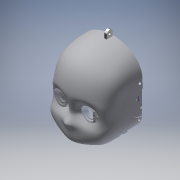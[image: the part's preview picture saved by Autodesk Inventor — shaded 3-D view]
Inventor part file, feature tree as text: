
AUTODESK INVENTOR PART (.ipt)
format: ipt  version: 2019 (Build 230136000, 136)  size: 8,056,320 bytes
history: native  units: in
note: dims shown in document units (in); Inventor stores cm internally (conversion verified against a paired STEP export)
features: sketch x29, extrude x22, other x18, plane x14, projected_geometry x7, mirror x6, surface_op x6, fillet x2, hole x2, thicken_offset x2, imported_body x2
ambient origin geometry x8: Origin, YZ Plane, XZ Plane, XY Plane, X Axis, Y Axis, Z Axis, Center Point
bodies: Solid6 (feature_tree), Solid2 (feature_tree)
feature tree (110):
  other  "rc_ist_009_p_077_09"
  other  "rc_ist_009_p_077_091"
  other  "Work Point1"
  other  "Work Point2"
  other  "Work Point3"
  other  "Work Point4"
  other  "Work Point5"
  other  "A_5"
  other  "A_6"
  other  "A_7"
  other  "A_8"
  other  "SIDE"
  other  "TOP"
  plane  "Work Plane4"
  plane  "Work Plane11"
  plane  "Work Plane7"
  plane  "Work Plane9"
  extrude  "Extrusion10"  Depth=0.9252in
  sketch  "Sketch11"  dims[d40=0.315in d41=0.315in]
  extrude  "Extrusion11"  Depth=0.315in
  plane  "Work Plane10"
  extrude  "Extrusion12"  Depth=1.063in TaperAngle=0.0deg
  mirror  "Mirror3"
  extrude  "Extrusion13"  Depth=1.8504in
  fillet  "Fillet1"  Radius=2.3622in
  fillet  "Fillet2"  Radius=0.3543in
  sketch  "Sketch15"  dims[d54=0.2756in d55=0.1969in d56=0.0in]
  extrude  "Extrusion14"  Depth=0.1969in TaperAngle=0.0deg
  extrude  "Extrusion15"  Depth=0.1969in TaperAngle=0.0deg
  extrude  "Extrusion16"  Depth=0.3937in
  extrude  "Extrusion17"  Depth=0.3937in
  extrude  "Extrusion18"  Depth=1.1811in
  extrude  "Extrusion19"  Depth=0.3937in
  hole  "Hole1"  [1 undecoded]
  hole  "Hole2"  [1 undecoded]
  extrude  "Extrusion22"  Depth=2.5591in
  extrude  "Extrusion23"  TaperAngle=150.0deg  [1 undecoded]
  extrude  "Extrusion24"  TaperAngle=60.0deg  [1 undecoded]
  extrude  "Extrusion25"  Depth=0.315in
  extrude  "Extrusion26"  Depth=0.3937in TaperAngle=0.0deg
  sketch  "Sketch34"  dims[d96=0.1969in d97=150.0deg]
  sketch  "3D Sketch2"
  surface_op  "Extend2"
  thicken_offset  "Thicken5"
  plane  "Work Plane12"
  extrude  "Extrusion27"  TaperAngle=150.0deg  [1 undecoded]
  plane  "Work Plane13"
  surface_op  "Extend3"
  thicken_offset  "Thicken6"
  mirror  "Mirror4"
  plane  "Work Plane14"
  plane  "Work Plane15"
  extrude  "Extrusion29"  TaperAngle=120.0deg  [1 undecoded]
  mirror  "Mirror5"
  plane  "Work Plane16"
  extrude  "Extrusion30"  TaperAngle=150.0deg  [1 undecoded]
  mirror  "Mirror6"
  extrude  "Extrusion31"  TaperAngle=120.0deg  [1 undecoded]
  plane  "Work Plane17"
  extrude  "Extrusion32"  Depth=0.7874in
  mirror  "Mirror8"
  extrude  "Extrusion33"  Depth=0.4331in
  extrude  "Extrusion34"  Depth=0.3937in
  mirror  "Mirror9"
  plane  "Work Plane19"
  plane  "Work Plane20"
  sketch  "3D Sketch1"
  other  "FRONT"
  imported_body  "Base1"
  imported_body  "Base2"
  plane  "Work Plane8"
  sketch  "Sketch10"  dims[d3=3.563in d35=0.9252in]
  sketch  "Sketch12"  dims[d42=0.315in d43=1.063in d44=0.0in]
  sketch  "Sketch13"  dims[d45=0.9252in d46=1.8504in d47=2.3622in d48=0.0in d49=0.3543in]
  sketch  "Sketch14"  dims[d50=0.3543in d52=0.1969in d53=0.0in]
  projected_geometry  "Projected Loop6"
  sketch  "Sketch16"  dims[d57=0.3937in d58=0.3937in]
  sketch  "Sketch17"  dims[d59=0.2362in d60=0.0in d61=0.3937in]
  projected_geometry  "Projected Loop7"
  projected_geometry  "Projected Loop8"
  projected_geometry  "Projected Loop9"
  sketch  "Sketch18"  dims[d62=180.0deg d63=1.1811in]
  projected_geometry  "Projected Loop10"
  sketch  "Sketch19"  dims[d64=90.0deg d65=0.3937in]
  projected_geometry  "Projected Loop11"
  sketch  "Sketch21"  dims[d66=90.0deg d67=3.937in d68=0.0in]
  sketch  "Sketch22"  dims[d73=0.3937in d75=3.937in d76=0.0in]
  sketch  "Sketch26"  dims[d77=3.937in d78=0.0in d82=2.5591in]
  sketch  "Sketch27"  dims[d83=2.5591in d84=150.0deg]
  sketch  "Sketch29"  dims[d85=0.315in d86=60.0deg]
  sketch  "Sketch30"  dims[d87=30.0deg d88=0.315in]
  sketch  "Sketch31"  dims[d89=60.0deg d90=0.3937in d91=0.0in]
  sketch  "Sketch32"  dims[d92=0.1969in d93=150.0deg]
  sketch  "Sketch33"  dims[d94=0.1969in d95=120.0deg]
  other  "Srf6"
  sketch  "Sketch35"  dims[d98=0.1969in d99=120.0deg]
  other  "Srf7"
  other  "Srf11"
  other  "Srf10"
  sketch  "Sketch38"  dims[d100=0.3937in d101=0.0in d108=0.7874in]
  sketch  "Sketch39"  dims[d109=0.2953in]
  sketch  "Sketch41"  dims[d110=0.2953in d111=0.2362in d112=0.1575in d113=0.0787in d114=90.0deg d115=0.315in d116=0.8108in d117=0.4331in]
  sketch  "Sketch42"  dims[d118=0.4724in d119=0.2362in d120=0.1575in d121=0.0787in d122=90.0deg d123=0.1969in d124=0.0in d127=0.3937in]
  sketch  "Sketch43"  dims[d128=0.1969in d129=0.0in]
  sketch  "Sketch44"  dims[d130=0.3937in d131=0.1969in d132=0.0in d133=0.7087in d134=0.1575in d135=0.0in d136=0.5906in d137=0.1575in d138=0.0in d139=0.3937in d140=0.0in d153=0.1969in d154=0.0in d158=0.1181in d160=0.3937in d161=-0.815in d162=0.0in d163=0.0in d165=0.8465in d166=1.0625in d169=0.1969in d170=0.0in d171=0.1575in d172=0.1575in d173=0.1575in d185=0.3937in d190=0.0in d191=-1.6063in d192=0.315in d193=0.3937in d194=0.0787in d195=0.3937in d196=0.0in d197=1.7913in d200=0.315in d201=0.3937in d202=0.0in d203=0.0787in d204=0.3937in d205=0.0in d213=0.1378in d214=0.1969in d215=0.1181in d216=0.3937in d217=0.0in d218=0.2362in d219=0.1181in d220=0.0in d221=0.1378in d222=0.1969in d223=0.1378in d224=0.0787in d225=0.0in d226=0.2362in d227=0.1181in d228=0.0in]
  projected_geometry  "Projected Loop12"
  surface_op  "Boundary Patch2"
  surface_op  "Boundary Patch3"
  surface_op  "Boundary Patch6"
  surface_op  "Boundary Patch7"
note: 8 required parameter values undecoded (feature->parameter linkage not recoverable at this tier; creation-order binding heuristic only, values carry confidence <= 0.55)
